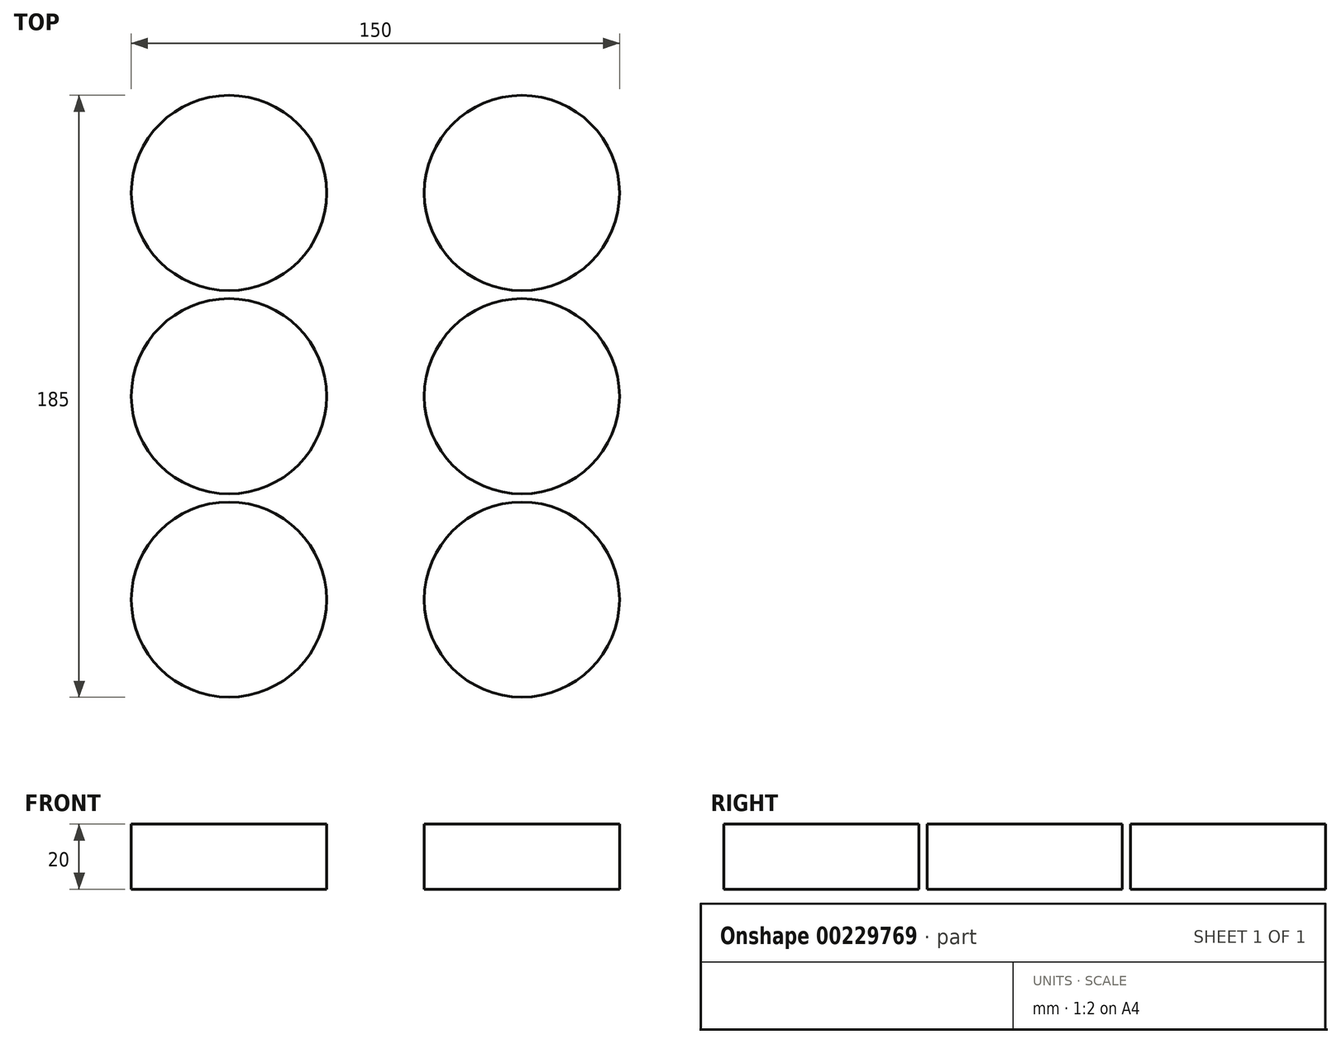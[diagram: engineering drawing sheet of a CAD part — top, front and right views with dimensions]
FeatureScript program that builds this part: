
annotation { "Feature Type Name" : "Feature", "Feature Type Description" : "" }
export const myFeature = defineFeature(function(context is Context, id is Id, definition is map)
    precondition{}
    {
        {
            var Q0;
            Q0=qCreatedBy(makeId("Top.planeOp"),FACE);
            var sketch = newSketch(context, id + "F0", { "sketchPlane" : qUnion([Q0])});
            skLineSegment(sketch, "E0.bottom", {"start": v(90, 97.5) * mm, "end": v(-90, 97.5) * mm, "construction": true});
            skLineSegment(sketch, "E0.top", {"start": v(90, -97.5) * mm, "end": v(-90, -97.5) * mm, "construction": true});
            skLineSegment(sketch, "E0.left", {"start": v(90, 97.5) * mm, "end": v(90, -97.5) * mm, "construction": true});
            skLineSegment(sketch, "E0.right", {"start": v(-90, 97.5) * mm, "end": v(-90, -97.5) * mm, "construction": true});
            skPoint(sketch, "E0.middle", {"position": v(0, 0) * mm});
            skCircle(sketch, "E1", {"center": v(-45, 62.5) * mm, "radius": 30 * mm});
            skLineSegment(sketch, "E2", {"start": v(0, 97.5) * mm, "end": v(0, -97.5) * mm, "construction": true});
            skCircle(sketch, "E3", {"center": v(-45, 0) * mm, "radius": 30 * mm});
            skCircle(sketch, "E4", {"center": v(-45, -62.5) * mm, "radius": 30 * mm});
            skCircle(sketch, "E5", {"center": v(45, 62.5) * mm, "radius": 30 * mm});
            skCircle(sketch, "E6", {"center": v(45, 0) * mm, "radius": 30 * mm});
            skCircle(sketch, "E7", {"center": v(45, -62.5) * mm, "radius": 30 * mm});
            skLineSegment(sketch, "E8", {"start": v(-90, -97.5) * mm, "end": v(0, -97.5) * mm, "construction": true});
            skPoint(sketch, "E9", {"position": v(-45, -97.5) * mm});
            skSolve(sketch);
        }
        {
            var Q0;
            Q0 = qSketchRegion(id + "F0", true);
            extrude(context, id + "F1", {"entities" : qUnion([Q0]), "depth" : 20 * mm});
        }
    });
